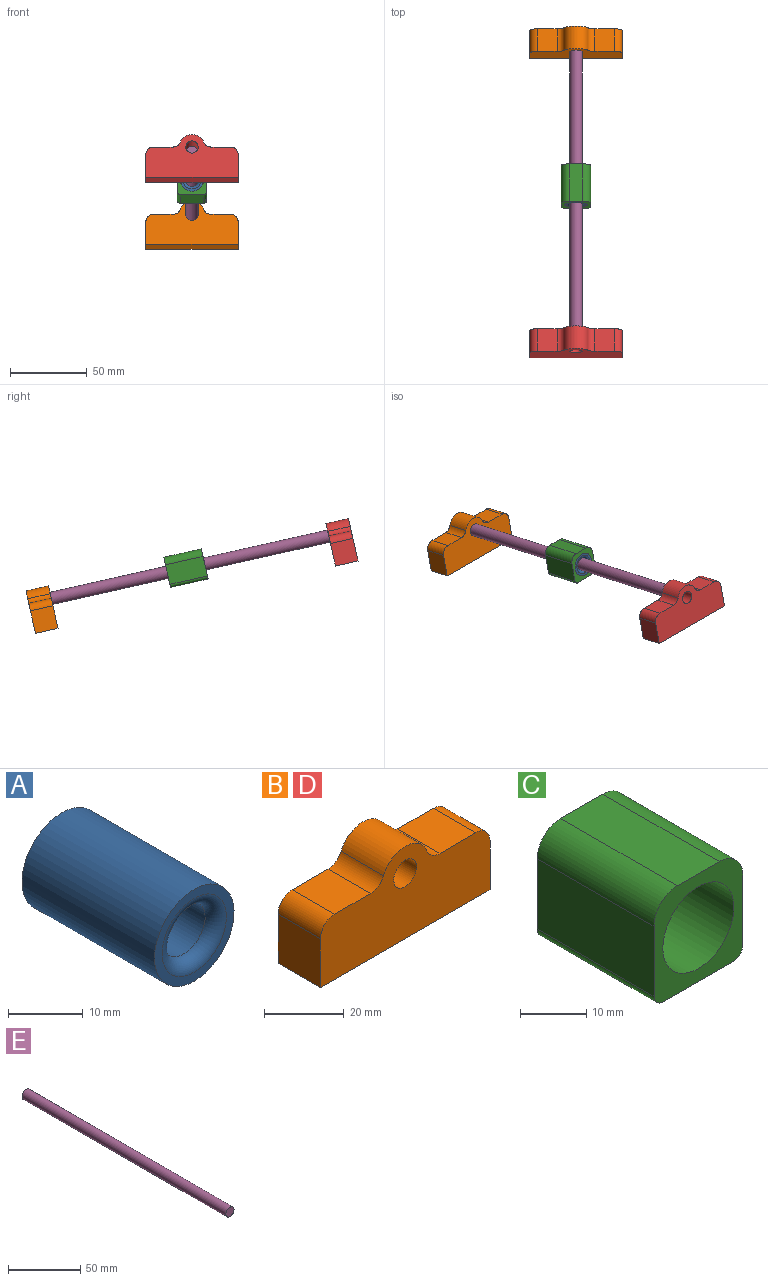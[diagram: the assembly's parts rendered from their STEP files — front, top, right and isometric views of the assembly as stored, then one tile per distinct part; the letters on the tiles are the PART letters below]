
ASSEMBLY  parts=5 mates=4
PART A: 6 faces, bbox 16.2x25x16.2 mm
  f0: cylinder r=4.05mm len=21mm, axis (0,1,0), area 534.4mm2, adj f4,f5
  f1: cylinder r=7.5mm len=25mm, axis (0,1,0), area 1178.1mm2, adj f2,f3
  f2: plane 15x15mm, normal (0,-1,0), area 61.7mm2, adj f1,f5
  f3: plane 15x15mm, normal (0,1,0), area 61.7mm2, adj f1,f4
  f4: torus R=6.05mm, axis (0,-1,0), area 94.3mm2, adj f0,f3
  f5: torus R=6.05mm, axis (0,-1,0), area 94.3mm2, adj f0,f2
PART B: 13 faces, bbox 60x15x28.3 mm
  f0: plane 60x15mm, normal (0,0,-1), area 900mm2, adj f1,f5,f7,f8
  f1: plane 15x15mm, normal (1,0,0), area 225mm2, adj f0,f7,f8,f11
  f2: plane 15x12.69mm, normal (0,0,1), area 190.3mm2, adj f7,f8,f9,f11
  f3: cylinder r=8.29mm len=15.36mm, axis (0,1,0), area 294.7mm2, adj f7,f8,f9,f10
  f4: plane 15x12.69mm, normal (0,0,1), area 190.3mm2, adj f7,f8,f10,f12
  f5: plane 15x15mm, normal (-1,0,0), area 225mm2, adj f0,f7,f8,f12
  f6: cylinder r=4.05mm len=15mm, axis (0,1,0), area 381.7mm2, adj f7,f8
  f7: plane 60x28.29mm, normal (0,-1,0), area 1251.1mm2, adj f0,f1,f2,f3,f4,f5,f6,f9
  f8: plane 60x28.29mm, normal (0,1,0), area 1251.1mm2, adj f0,f1,f2,f3,f4,f5,f6,f9
  f9: cylinder r=5mm len=15mm, axis (0,1,0), area 88.9mm2, adj f2,f3,f7,f8
  f10: cylinder r=5mm len=15mm, axis (0,1,0), area 88.9mm2, adj f3,f4,f7,f8
  f11: cylinder r=5mm len=15mm, axis (0,1,0), area 117.8mm2, adj f1,f2,f7,f8
  f12: cylinder r=5mm len=15mm, axis (0,1,0), area 117.8mm2, adj f4,f5,f7,f8
PART C: 15 faces, bbox 19x25x20 mm
  f0: cylinder r=2mm len=25mm, axis (0,1,0), area 68.7mm2, adj f1,f6,f9,f10,f11,f12,f13
  f1: plane 25x13mm, normal (1,0,0), area 290.5mm2, adj f0,f8,f9,f10,f11,f12,f14
  f2: plane 25x9mm, normal (0,0,1), area 225mm2, adj f3,f8,f9,f10
  f3: cylinder r=5mm len=25mm, axis (0,1,0), area 196.3mm2, adj f2,f4,f9,f10
  f4: plane 25x13mm, normal (-1,0,0), area 325mm2, adj f3,f5,f9,f10
  f5: cylinder r=2mm len=25mm, axis (0,1,0), area 78.5mm2, adj f4,f6,f9,f10
  f6: plane 25x15mm, normal (0,0,-1), area 375mm2, adj f0,f5,f9,f10
  f7: cylinder r=7.6mm len=25mm, axis (0,1,0), area 1193.8mm2, adj f9,f10
  f8: cylinder r=5mm len=25mm, axis (0,1,0), area 196.3mm2, adj f1,f2,f9,f10
  f9: plane 20x19mm, normal (0,-1,0), area 186.1mm2, adj f0,f1,f2,f3,f4,f5,f6,f7
  f10: plane 20x19mm, normal (0,1,0), area 186.1mm2, adj f0,f1,f2,f3,f4,f5,f6,f7
  f11: plane 9.09x7.15mm, normal (0,-0.79,-0.62), area 10.9mm2, adj f0,f1,f13,f14
  f12: plane 9.09x7.15mm, normal (0,0.79,0.62), area 10.9mm2, adj f0,f1,f13,f14
  f13: plane 11.84x9.09mm, normal (1,0,0), area 42.7mm2, adj f0,f11,f12,f14
  f14: plane 4.69x1mm, normal (0,0,-1), area 4.7mm2, adj f1,f11,f12,f13
PART D: same geometry as B
PART E: 3 faces, bbox 8x200x8 mm
  f0: cylinder r=4mm len=200mm, axis (0,1,0), area 5026.5mm2, adj f1,f2
  f1: plane 8x8mm, normal (0,-1,0), area 50.3mm2, adj f0
  f2: plane 8x8mm, normal (0,1,0), area 50.3mm2, adj f0
PLACE A rot(axis=(-1,0,0),12.6deg) t=(-68.31,-168.09,-39.27)mm
PLACE B rot(axis=(-1,0,0),12.6deg) t=(-88.98,-70.72,-26.86)mm
PLACE C rot(axis=(-1,0,0),12.6deg) t=(-101.96,-168.66,-41.84)mm
PLACE D rot(axis=(-1,0,0),12.6deg) t=(-88.98,-265.87,16.92)mm
PLACE E rot(axis=(1,0,0),167.4deg) t=(-38.49,-252.49,76.56)mm
MATE revolute E.f0 <-> B.f3  axis (0,0.98,-0.22) through (-87.25,-66.34,-7.34)mm
MATE revolute D.f3 <-> E.f0  axis (0,0.98,-0.22) through (-87.25,-261.49,36.44)mm
MATE slider A.f0 <-> E.f0  axis (0,-0.98,0.22) through (-87.25,-180.78,18.33)mm
MATE planar C.f7 <-> A.f0  axis (0,0.98,-0.22) through (-87.25,-168.59,15.6)mm
